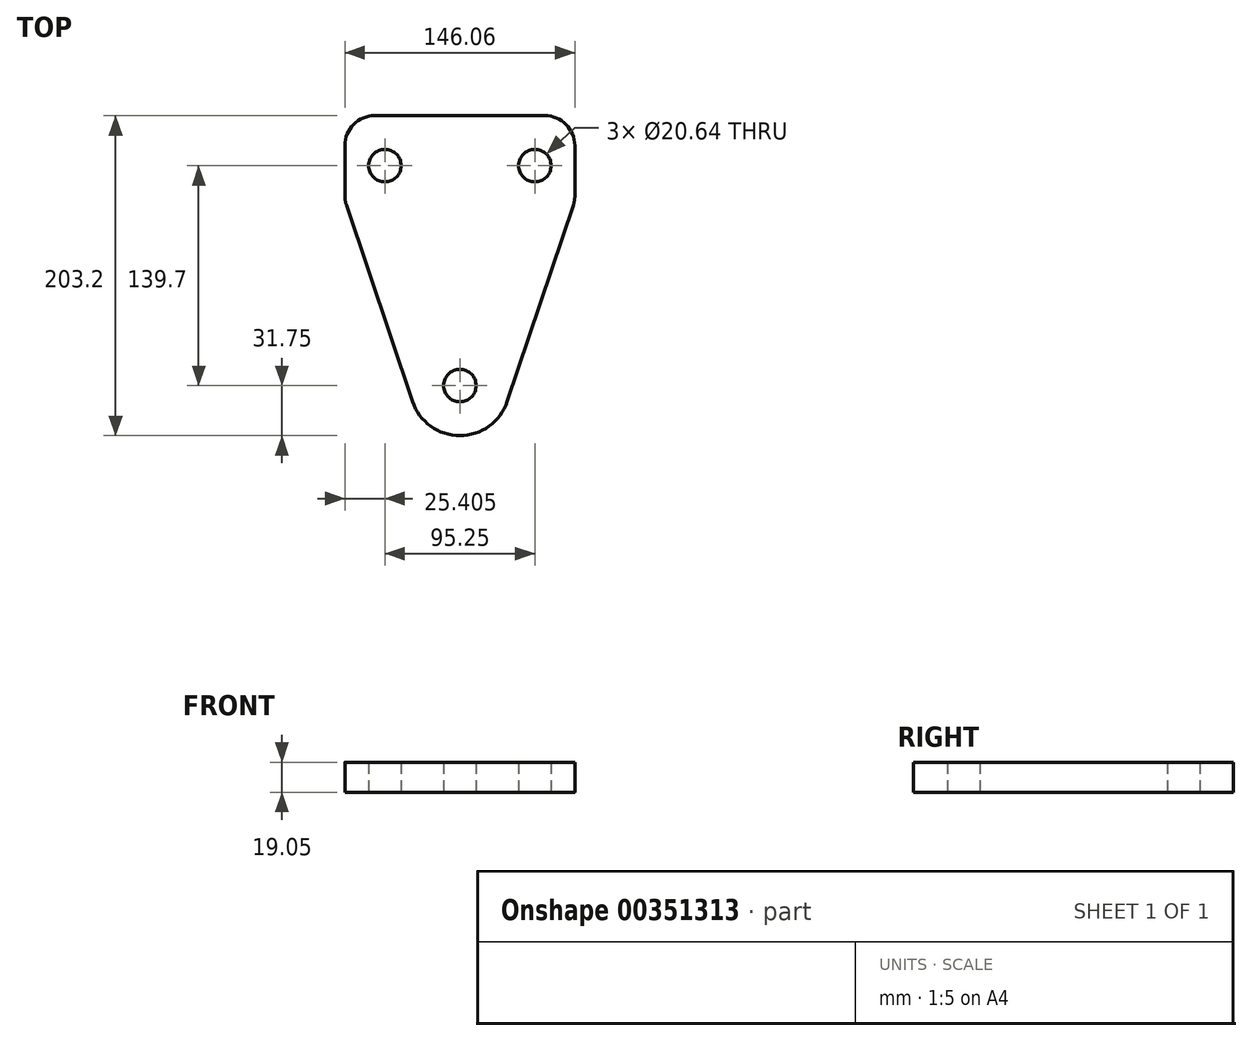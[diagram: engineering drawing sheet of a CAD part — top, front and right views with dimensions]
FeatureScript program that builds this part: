
annotation { "Feature Type Name" : "Feature", "Feature Type Description" : "" }
export const myFeature = defineFeature(function(context is Context, id is Id, definition is map)
    precondition{}
    {
        {
            var Q0;
            Q0=qCreatedBy(makeId("Top.planeOp"),FACE);
            var sketch = newSketch(context, id + "F0", { "sketchPlane" : qUnion([Q0])});
            skCircle(sketch, "E0", {"center": v(0, 0) * mm, "radius": 10.32 * mm});
            skCircle(sketch, "E1", {"center": v(-47.63, 139.7) * mm, "radius": 10.32 * mm});
            skCircle(sketch, "E2", {"center": v(47.63, 139.7) * mm, "radius": 10.32 * mm});
            skLineSegment(sketch, "E3", {"start": v(30.1, -10.12) * mm, "end": v(72.03, 114.58) * mm});
            skLineSegment(sketch, "E4", {"start": v(73.03, 120.65) * mm, "end": v(73.03, 152.4) * mm});
            skLineSegment(sketch, "E5", {"start": v(-73.03, 152.4) * mm, "end": v(-73.03, 120.65) * mm});
            skLineSegment(sketch, "E6", {"start": v(-72.03, 114.58) * mm, "end": v(-30.1, -10.12) * mm});
            skPoint(sketch, "E7.visualSharp", {"position": v(-73.03, 171.45) * mm});
            skArc(sketch, "E7.filletArc", {"start": v(-53.98, 171.45) * mm, "mid": v(-67.45, 165.87) * mm, "end": v(-73.03, 152.4) * mm});
            skPoint(sketch, "E8.visualSharp", {"position": v(73.03, 171.45) * mm});
            skArc(sketch, "E8.filletArc", {"start": v(73.03, 152.4) * mm, "mid": v(67.45, 165.87) * mm, "end": v(53.98, 171.45) * mm});
            skArc(sketch, "E9.filletArc", {"start": v(-73.03, 120.65) * mm, "mid": v(-72.77, 117.57) * mm, "end": v(-72.03, 114.58) * mm});
            skArc(sketch, "E10.filletArc", {"start": v(72.03, 114.58) * mm, "mid": v(72.77, 117.57) * mm, "end": v(73.03, 120.65) * mm});
            skArc(sketch, "E11", {"start": v(30.1, -10.12) * mm, "mid": v(0, -31.75) * mm, "end": v(-30.1, -10.12) * mm});
            skLineSegment(sketch, "E12", {"start": v(-53.98, 171.45) * mm, "end": v(53.98, 171.45) * mm});
            skLineSegment(sketch, "E13", {"start": v(0, 0) * mm, "end": v(0, 171.45) * mm, "construction": true});
            skLineSegment(sketch, "E14", {"start": v(47.63, 139.7) * mm, "end": v(-47.63, 139.7) * mm, "construction": true});
            skLineSegment(sketch, "E15", {"start": v(53.98, 120.65) * mm, "end": v(-53.98, 120.65) * mm, "construction": true});
            skLineSegment(sketch, "E16", {"start": v(-72.03, 114.58) * mm, "end": v(-53.98, 120.65) * mm, "construction": true});
            skLineSegment(sketch, "E17", {"start": v(53.98, 120.65) * mm, "end": v(73.03, 120.65) * mm, "construction": true});
            skLineSegment(sketch, "E18", {"start": v(0, 0) * mm, "end": v(-30.1, -10.12) * mm, "construction": true});
            skLineSegment(sketch, "E19", {"start": v(-53.98, 152.4) * mm, "end": v(-53.98, 171.45) * mm, "construction": true});
            skLineSegment(sketch, "E20", {"start": v(-53.98, 152.4) * mm, "end": v(-73.03, 152.4) * mm, "construction": true});
            skLineSegment(sketch, "E21", {"start": v(53.98, 152.4) * mm, "end": v(73.02, 152.4) * mm, "construction": true});
            skLineSegment(sketch, "E22", {"start": v(53.98, 152.4) * mm, "end": v(53.98, 171.45) * mm, "construction": true});
            skLineSegment(sketch, "E23", {"start": v(30.1, -10.12) * mm, "end": v(0, 0) * mm, "construction": true});
            skLineSegment(sketch, "E24", {"start": v(72.03, 114.58) * mm, "end": v(53.98, 120.65) * mm, "construction": true});
            skSolve(sketch);
        }
        {
            var Q0;
            Q0=makeQuery(id+"F0.imprint","IMPRINT",FACE,{"disambiguationData":[TD([[makeQuery(id+"F0.imprint","IMPRINT",EDGE,{"derivedFrom":sQuery(id+"F0.wireOp",EDGE,"E0")}),-1.0]])]});
            extrude(context, id + "F1", {"entities" : qUnion([Q0]), "depth" : 19.05 * mm});
        }
    });
